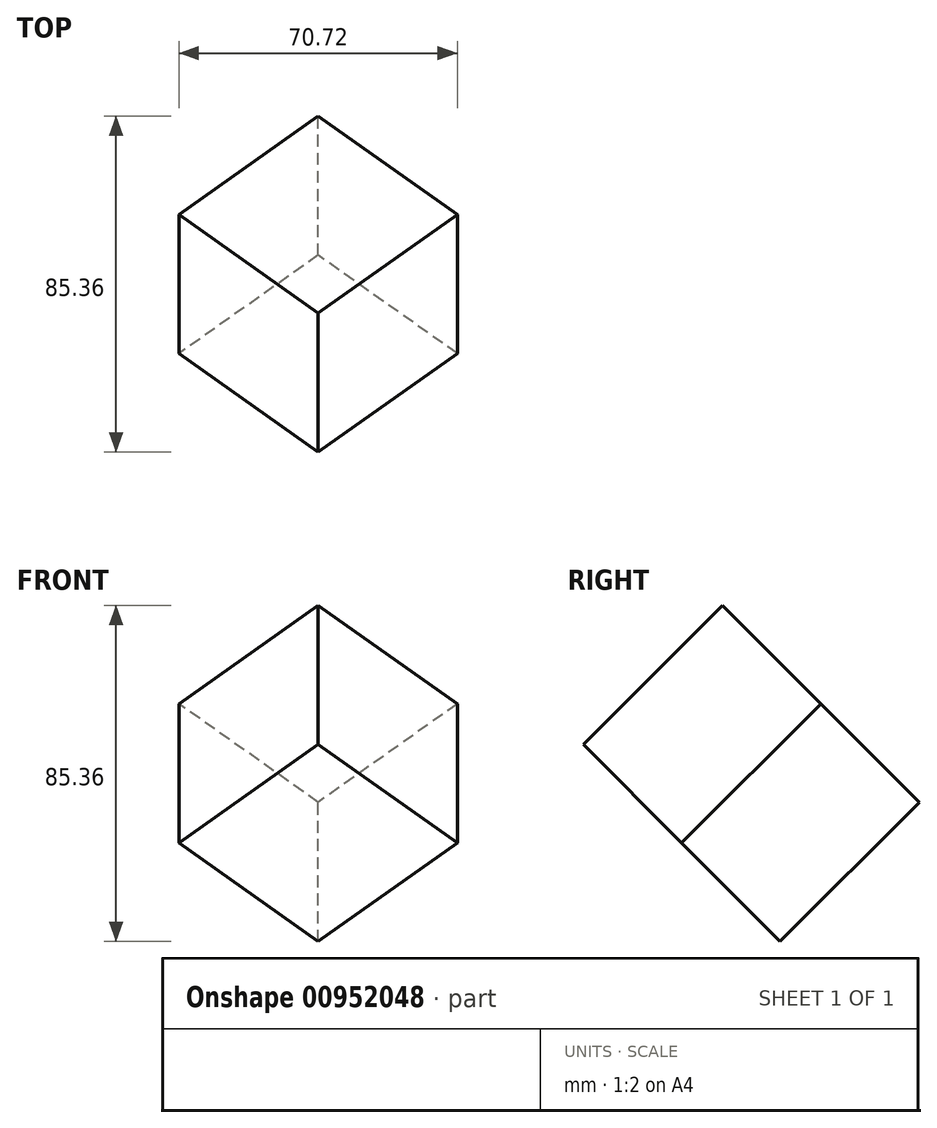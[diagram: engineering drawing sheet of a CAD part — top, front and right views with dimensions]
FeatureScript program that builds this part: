
annotation { "Feature Type Name" : "Feature", "Feature Type Description" : "" }
export const myFeature = defineFeature(function(context is Context, id is Id, definition is map)
    precondition{}
    {
        {
            assignVariable(context, id + "F0", {"name" : "SideLength", "anyValue" : 50});
        }
        {
            var Q0;
            Q0=qCreatedBy(makeId("Top.planeOp"),FACE);
            var sketch = newSketch(context, id + "F1", { "sketchPlane" : qUnion([Q0])});
            skLineSegment(sketch, "E0.bottom", {"start": v(25, -25) * mm, "end": v(-25, -25) * mm});
            skLineSegment(sketch, "E0.top", {"start": v(25, 25) * mm, "end": v(-25, 25) * mm});
            skLineSegment(sketch, "E0.left", {"start": v(25, -25) * mm, "end": v(25, 25) * mm});
            skLineSegment(sketch, "E0.right", {"start": v(-25, -25) * mm, "end": v(-25, 25) * mm});
            skPoint(sketch, "E0.middle", {"position": v(0, 0) * mm});
            skSolve(sketch);
        }
        {
            var Q0;
            Q0 = qSketchRegion(id + "F1", true);
            extrude(context, id + "F2", {"entities" : qUnion([Q0]), "endBound" : BoundingType.SYMMETRIC, "depth" : (getVariable(context, 'SideLength')) * mm, "offsetDistance" : 25 * mm});
        }
        {
            var Q0;
            Q0=qCreatedBy(makeId("Right.planeOp"),FACE);
            var sketch = newSketch(context, id + "F3", { "sketchPlane" : qUnion([Q0])});
            skLineSegment(sketch, "E1", {"start": v(-25, 0) * mm, "end": v(25, 0) * mm, "construction": true});
            skSolve(sketch);
        }
        {
            var Q0;
            Q0=makeQuery(id+"F2.opExtrude","SWEPT_BODY",BODY,{"disambiguationData":[OSD([sQuery(id+"F1.wireOp",EDGE,"E0.bottom"),sQuery(id+"F1.wireOp",EDGE,"E0.top"),sQuery(id+"F1.wireOp",EDGE,"E0.left"),sQuery(id+"F1.wireOp",EDGE,"E0.right")])]});
            var Q1;
            Q1=sQuery(id+"F3.wireOp",EDGE,"E1");
            transform(context, id + "F4", {"entities" : qUnion([Q0]), "transformType" : TransformType.ROTATION, "transformAxis" : qUnion([Q1]), "angle" : 45 * degree, "makeCopy" : false});
        }
        {
            var Q0;
            Q0=qCreatedBy(makeId("Front.planeOp"),FACE);
            var sketch = newSketch(context, id + "F5", { "sketchPlane" : qUnion([Q0])});
            skLineSegment(sketch, "E2", {"start": v(-25, 0) * mm, "end": v(25, 0) * mm, "construction": true});
            skSolve(sketch);
        }
        {
            var Q0;
            Q0=makeQuery(id+"F2.opExtrude","SWEPT_BODY",BODY,{"disambiguationData":[OSD([sQuery(id+"F1.wireOp",EDGE,"E0.bottom"),sQuery(id+"F1.wireOp",EDGE,"E0.top"),sQuery(id+"F1.wireOp",EDGE,"E0.left"),sQuery(id+"F1.wireOp",EDGE,"E0.right")])]});
            var Q1;
            Q1=sQuery(id+"F5.wireOp",EDGE,"E2");
            transform(context, id + "F6", {"entities" : qUnion([Q0]), "transformType" : TransformType.ROTATION, "transformAxis" : qUnion([Q1]), "angle" : 45 * degree, "makeCopy" : false});
        }
    });
